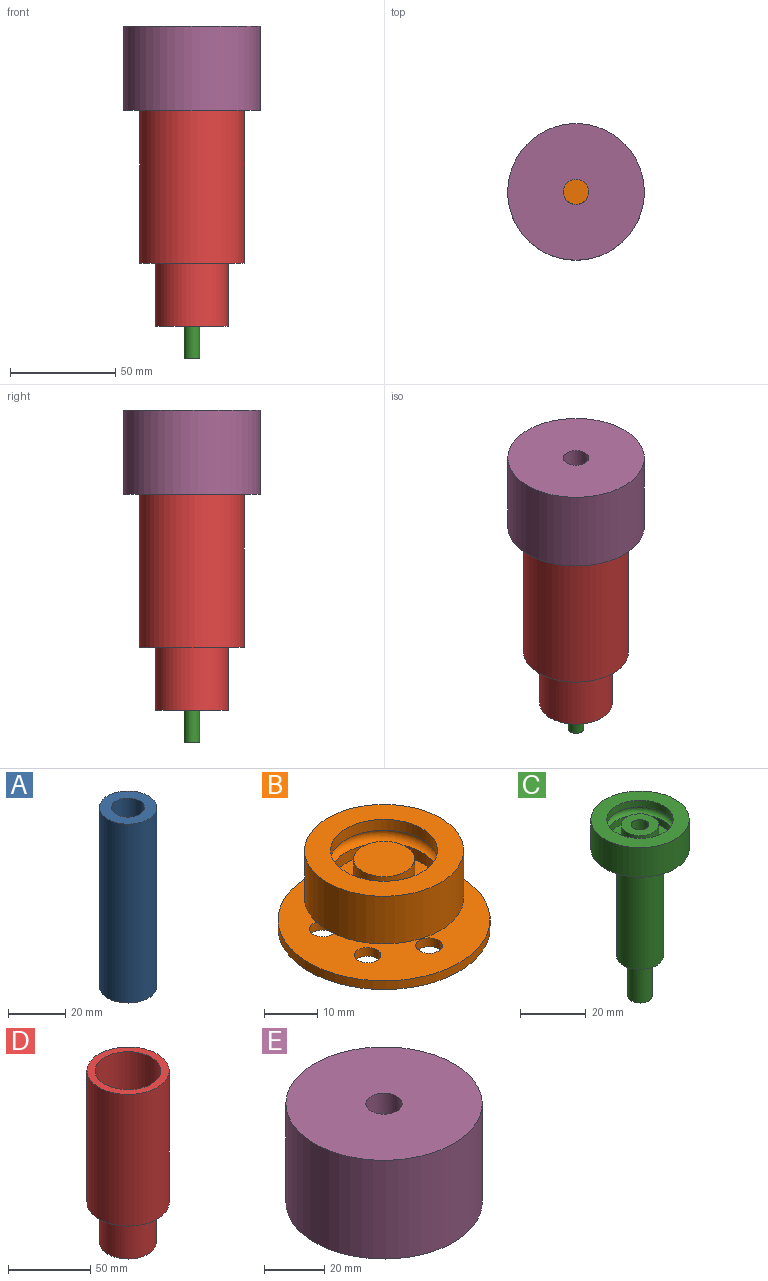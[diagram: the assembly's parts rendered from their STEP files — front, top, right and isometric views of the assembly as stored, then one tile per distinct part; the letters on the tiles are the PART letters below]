
ASSEMBLY  parts=5 mates=8
PART A: 4 faces, bbox 20x20x76.3 mm
  f0: cylinder r=5.75mm len=76.3mm, axis (0,0,-1), area 2756.6mm2, adj f2,f3
  f1: cylinder r=10mm len=76.3mm, axis (0,0,-1), area 4794.1mm2, adj f2,f3
  f2: plane 20x20mm, normal (0,0,1), area 210.3mm2, adj f0,f1
  f3: plane 20x20mm, normal (0,0,-1), area 210.3mm2, adj f0,f1
PART B: 19 faces, bbox 40x40x18 mm
  f0: cylinder r=10.1mm len=20.2mm, axis (0,0,-1), area 158.7mm2, adj f13,f14
  f1: cylinder r=2.5mm len=5mm, axis (0,0,-1), area 31.4mm2, adj f8,f9
  f2: cylinder r=2.5mm len=5mm, axis (0,0,-1), area 31.4mm2, adj f8,f9
  f3: cylinder r=2.5mm len=5mm, axis (0,0,-1), area 31.4mm2, adj f8,f9
  f4: cylinder r=2.5mm len=5mm, axis (0,0,-1), area 31.4mm2, adj f8,f9
  f5: cylinder r=2.5mm len=5mm, axis (0,0,-1), area 31.4mm2, adj f8,f9
  f6: cylinder r=2.5mm len=5mm, axis (0,0,-1), area 31.4mm2, adj f8,f9
  f7: cylinder r=20mm len=40mm, axis (0,0,-1), area 251.3mm2, adj f8,f9
  f8: plane 40x40mm, normal (0,0,1), area 1060.3mm2, adj f1,f2,f3,f4,f5,f6,f7,f10
  f9: plane 40x40mm, normal (0,0,-1), area 1138.8mm2, adj f1,f2,f3,f4,f5,f6,f7
  f10: cylinder r=5mm len=10mm, axis (0,0,-1), area 157.1mm2, adj f8,f12
  f11: cylinder r=15mm len=30mm, axis (0,0,-1), area 1036.7mm2, adj f12,f13
  f12: plane 30x30mm, normal (0,0,-1), area 628.3mm2, adj f10,f11
  f13: plane 30x30mm, normal (0,0,1), area 386.4mm2, adj f0,f11
  f14: torus R=10.1mm, axis (0,0,1), area 327.3mm2, adj f0,f18
  f15: plane 11.5x11.5mm, normal (0,0,1), area 103.9mm2, adj f16
  f16: cylinder r=5.75mm len=11.5mm, axis (0,0,-1), area 216.8mm2, adj f15,f17
  f17: plane 20.2x20.2mm, normal (0,0,1), area 216.6mm2, adj f16,f18
  f18: cylinder r=10.1mm len=20.2mm, axis (0,0,-1), area 158.7mm2, adj f14,f17
PART C: 16 faces, bbox 30x30x66 mm
  f0: plane 14.4x14.4mm, normal (0,0,-1), area 64.9mm2, adj f13,f15
  f1: plane 7.63x7.63mm, normal (0,0,-1), area 2.7mm2, adj f5,f15
  f2: cylinder r=15mm len=30mm, axis (0,0,-1), area 1036.7mm2, adj f11,f14
  f3: cylinder r=10.1mm len=20.2mm, axis (0,0,-1), area 158.7mm2, adj f11,f12
  f4: cylinder r=2.7mm len=64mm, axis (0,0,-1), area 1085.7mm2, adj f6,f9
  f5: cylinder r=3.7mm len=15mm, axis (0,0,-1), area 348.7mm2, adj f1,f6
  f6: plane 7.4x7.4mm, normal (0,0,-1), area 20.1mm2, adj f4,f5
  f7: plane 20.2x20.2mm, normal (0,0,1), area 216.6mm2, adj f8,f10
  f8: cylinder r=5.75mm len=11.5mm, axis (0,0,-1), area 216.8mm2, adj f7,f9
  f9: plane 11.5x11.5mm, normal (0,0,1), area 81mm2, adj f4,f8
  f10: cylinder r=10.1mm len=20.2mm, axis (0,0,-1), area 158.7mm2, adj f7,f12
  f11: plane 30x30mm, normal (0,0,1), area 386.4mm2, adj f2,f3
  f12: torus R=10.1mm, axis (0,0,1), area 327.3mm2, adj f3,f10
  f13: cylinder r=7.2mm len=40mm, axis (0,0,-1), area 1809.6mm2, adj f0,f14
  f14: plane 30x30mm, normal (0,0,-1), area 544mm2, adj f2,f13
  f15: torus R=4.7mm, axis (0,0,1), area 82.1mm2, adj f0,f1
PART D: 8 faces, bbox 50x50x128 mm
  f0: plane 40x40mm, normal (0,0,1), area 705.1mm2, adj f1,f6
  f1: cylinder r=13.25mm len=35mm, axis (0,0,-1), area 2913.8mm2, adj f0,f3
  f2: cylinder r=17.25mm len=34.5mm, axis (0,0,-1), area 3251.5mm2, adj f3,f5
  f3: plane 34.5x34.5mm, normal (0,0,-1), area 383.3mm2, adj f1,f2
  f4: cylinder r=25mm len=98mm, axis (0,0,-1), area 15393.8mm2, adj f5,f7
  f5: plane 50x50mm, normal (0,0,-1), area 1028.7mm2, adj f2,f4
  f6: cylinder r=20mm len=93mm, axis (0,0,-1), area 11686.7mm2, adj f0,f7
  f7: plane 50x50mm, normal (0,0,1), area 706.9mm2, adj f4,f6
PART E: 11 faces, bbox 65x65x40 mm
  f0: cylinder r=6mm len=12mm, axis (0,0,-1), area 328mm2, adj f6,f10
  f1: cylinder r=25mm len=50mm, axis (0,0,-1), area 34.6mm2, adj f5,f7
  f2: cylinder r=25mm len=50mm, axis (0,0,-1), area 3333.2mm2, adj f4,f7
  f3: cylinder r=32.5mm len=65mm, axis (0,0,-1), area 8168.1mm2, adj f4,f6
  f4: plane 65x65mm, normal (0,0,-1), area 1354.8mm2, adj f2,f3
  f5: plane 50x50mm, normal (0,0,-1), area 675.2mm2, adj f1,f8
  f6: plane 65x65mm, normal (0,0,1), area 3205.2mm2, adj f0,f3
  f7: torus R=25mm, axis (0,0,1), area 918.2mm2, adj f1,f2
  f8: cylinder r=20.25mm len=40.5mm, axis (0,0,-1), area 165.4mm2, adj f5,f9
  f9: plane 40.5x40.5mm, normal (0,0,-1), area 270.4mm2, adj f8,f10
  f10: cone r=6mm half-angle=67.4deg, axis (0,0,-1), area 980.2mm2, adj f0,f9
PLACE A rot(axis=(0,0,1),48.1deg) t=(0.05,0.11,-21.88)mm
PLACE B rot(axis=(0.99,-0.11,0),180deg) t=(0.05,0.11,64.42)mm
PLACE C rot(axis=(0,0,1),83.7deg) t=(0.05,0.11,-79.88)mm
PLACE D t=(0.05,0.11,-64.88)mm fixed
PLACE E rot(axis=(0,0,-1),90deg) t=(0.05,0.11,38.12)mm
MATE cylindrical C.f13 <-> D.f1  axis (0,0,-1) through (0.05,0.11,-44.88)mm
MATE planar E.f0 <-> D.f1  axis (0,0,-1) through (0.05,0.11,63.12)mm
MATE cylindrical E.f1 <-> B.f7  axis (0,0,-1) through (0.05,0.11,38.12)mm
MATE cylindrical B.f7 <-> D.f6  axis (0,0,-1) through (0.05,0.11,46.42)mm
MATE planar A.f1 <-> B.f0  axis (0,0,1) through (0.05,0.11,54.42)mm
MATE cylindrical A.f1 <-> D.f4  axis (0,0,-1) through (0.05,0.11,16.27)mm
MATE planar C.f13 <-> D.f4  axis (0,0,-1) through (0.05,0.11,-64.88)mm
MATE planar C.f3 <-> A.f1  axis (0,0,1) through (0.05,0.11,-21.88)mm
